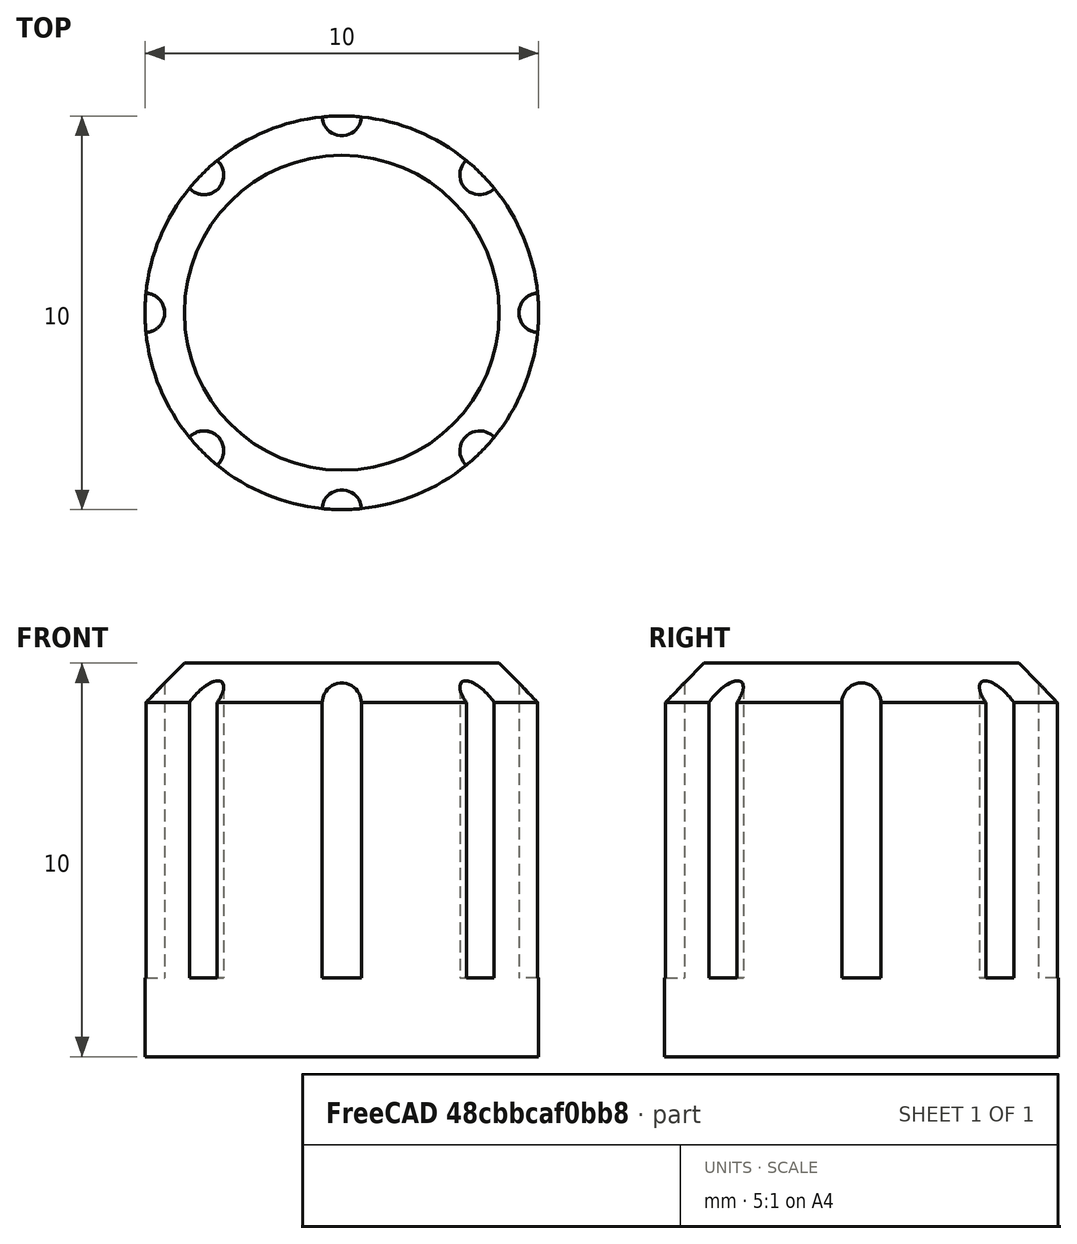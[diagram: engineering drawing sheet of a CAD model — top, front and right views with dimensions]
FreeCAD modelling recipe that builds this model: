
FCSTD DOCUMENT  (FreeCAD 0.21R33694 (Git))
Label: OJT1_T12R01_boton
License: All rights reserved
LicenseURL: http://en.wikipedia.org/wiki/All_rights_reserved
objects: Part::Cylinder×9, Part::Cut×8, Part::Chamfer×1
note: 18 computed .brp shape members not serialized (recipe doc carries the construction recipe); baked Part::Feature solids carry a one-line shape summary decoded from their .brp

FEATURE [Part::Cylinder] Cylinder
  Angle = 360
  AttacherType = Attacher::AttachEngine3D
  FirstAngle = 0
  Height = 10
  Radius = 5
  SecondAngle = 0
FEATURE [Part::Chamfer] Chamfer
  Base = -> Cylinder
  Edges = 1 edges r=1: [Edge3]
FEATURE [Part::Cylinder] Cylinder001
  Angle = 360
  AttacherType = Attacher::AttachEngine3D
  FirstAngle = 0
  Height = 10
  Placement = pos=(5,0,2) rot=(0,0,1;0rad)
  Radius = 0.5
  SecondAngle = 0
FEATURE [Part::Cylinder] Cylinder002
  Angle = 360
  AttacherType = Attacher::AttachEngine3D
  FirstAngle = 0
  Height = 10
  Placement = pos=(-5,0,2) rot=(0,0,1;0rad)
  Radius = 0.5
  SecondAngle = 0
FEATURE [Part::Cylinder] Cylinder003
  Angle = 360
  AttacherType = Attacher::AttachEngine3D
  FirstAngle = 0
  Height = 10
  Placement = pos=(0,5,2) rot=(0,0,1;0rad)
  Radius = 0.5
  SecondAngle = 0
FEATURE [Part::Cylinder] Cylinder004
  Angle = 360
  AttacherType = Attacher::AttachEngine3D
  FirstAngle = 0
  Height = 10
  Placement = pos=(0,-5,2) rot=(0,0,1;0rad)
  Radius = 0.5
  SecondAngle = 0
FEATURE [Part::Cylinder] Cylinder005
  Angle = 360
  AttacherType = Attacher::AttachEngine3D
  FirstAngle = 0
  Height = 10
  Placement = pos=(3.5,-3.5,2) rot=(0,0,1;0rad)
  Radius = 0.5
  SecondAngle = 0
FEATURE [Part::Cylinder] Cylinder006
  Angle = 360
  AttacherType = Attacher::AttachEngine3D
  FirstAngle = 0
  Height = 10
  Placement = pos=(-3.5,3.5,2) rot=(0,0,1;0rad)
  Radius = 0.5
  SecondAngle = 0
FEATURE [Part::Cylinder] Cylinder007
  Angle = 360
  AttacherType = Attacher::AttachEngine3D
  FirstAngle = 0
  Height = 10
  Placement = pos=(3.5,3.5,2) rot=(0,0,1;0rad)
  Radius = 0.5
  SecondAngle = 0
FEATURE [Part::Cylinder] Cylinder008
  Angle = 360
  AttacherType = Attacher::AttachEngine3D
  FirstAngle = 0
  Height = 10
  Placement = pos=(-3.5,-3.5,2) rot=(0,0,1;0rad)
  Radius = 0.5
  SecondAngle = 0
FEATURE [Part::Cut] Cut
  Base = -> Chamfer
  Refine = true
  Tool = -> Cylinder001
FEATURE [Part::Cut] Cut001
  Base = -> Cut
  Refine = true
  Tool = -> Cylinder008
FEATURE [Part::Cut] Cut002
  Base = -> Cut001
  Refine = true
  Tool = -> Cylinder007
FEATURE [Part::Cut] Cut003
  Base = -> Cut002
  Refine = true
  Tool = -> Cylinder006
FEATURE [Part::Cut] Cut004
  Base = -> Cut003
  Refine = true
  Tool = -> Cylinder005
FEATURE [Part::Cut] Cut005
  Base = -> Cut004
  Refine = true
  Tool = -> Cylinder004
FEATURE [Part::Cut] Cut006
  Base = -> Cut005
  Refine = true
  Tool = -> Cylinder003
FEATURE [Part::Cut] Cut007
  Base = -> Cut006
  Refine = true
  Tool = -> Cylinder002
